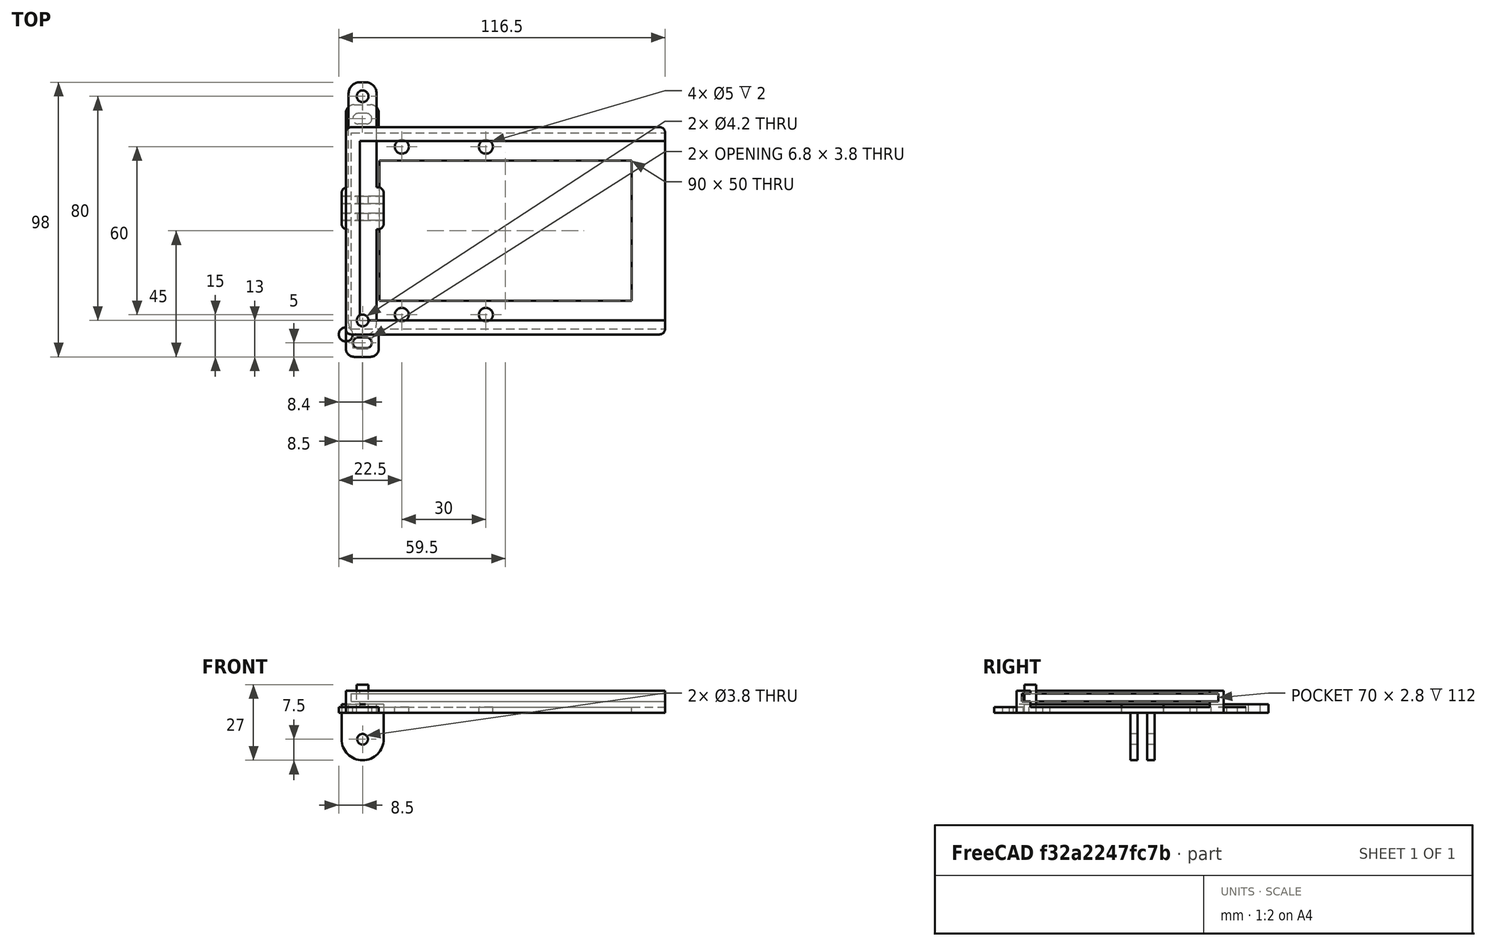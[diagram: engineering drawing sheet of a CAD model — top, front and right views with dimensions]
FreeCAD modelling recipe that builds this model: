
FCSTD DOCUMENT  (FreeCAD 0.19R23578 (Git))
Label: solar_110x70
License: All rights reserved
LicenseURL: http://en.wikipedia.org/wiki/All_rights_reserved
objects: Part::Box×6, Part::Fillet×3, Part::MultiFuse×3, Part::Cylinder×2, Part::FeaturePython×2, Part::Feature×2, Part::Cut×2, App::Part×2, Spreadsheet::Sheet×1
note: 18 computed .brp shape members not serialized (recipe doc carries the construction recipe); baked Part::Feature solids carry a one-line shape summary decoded from their .brp

FEATURE [Part::Box] Box  label="outer cube"
  AttacherType = Attacher::AttachEngine3D
  Height = 7.8
  Length = 114
  Width = 74
  expr: Height = <<p>>.bottom + <<p>>.bottom_space + <<p>>.size_z + <<p>>.top
  expr: Length = <<p>>.size_x + 2 * <<p>>.wall
  expr: Width = <<p>>.size_y + 2 * <<p>>.wall
FEATURE [Spreadsheet::Sheet] Spreadsheet  label="p"
  cells = A1=size_x; B1(size_x)==110mm; A2=size_y; B2(size_y)==70mm; A3=size_z; B3(size_z)==2.8mm; A4=wall; B4(wall)==2mm; A5=bottom_space; B5(bottom_space)==2mm; A6=top; B6(top)==1mm; A7=bottom; B7(bottom)==2mm; A8=pad; B8(pad)==10mm; A9=wire_hole_size; B9(wire_hole_r)==2.5mm; A10=side_lane; B10(side_lane)==3mm
FEATURE [Part::Box] Box001  label="bottom space cube"
  AttacherType = Attacher::AttachEngine3D
  Height = 2
  Length = 109
  Placement = pos=(5,5,2) rot=(0,0,1;0rad)
  Width = 64
  expr: Width = <<p>>.size_y - 2 * <<p>>.side_lane
  expr: Length = <<p>>.size_x - <<p>>.side_lane + <<p>>.wall
  expr: Height = <<p>>.bottom_space
  expr: .Placement.Base.x = <<p>>.wall + <<p>>.side_lane
  expr: .Placement.Base.y = <<p>>.wall + <<p>>.side_lane
  expr: .Placement.Base.z = <<p>>.bottom
FEATURE [Part::Box] Box002  label="panel extract cube"
  AttacherType = Attacher::AttachEngine3D
  Height = 2.8
  Length = 112
  Placement = pos=(2,2,4) rot=(0,0,1;0rad)
  Width = 70
  expr: .Placement.Base.z = <<p>>.bottom + <<p>>.bottom_space
  expr: .Placement.Base.y = <<p>>.wall
  expr: .Placement.Base.x = <<p>>.wall
  expr: Height = <<p>>.size_z
  expr: Length = <<p>>.size_x + <<p>>.wall
  expr: Width = <<p>>.size_y
FEATURE [Part::Box] Box003  label="panel face extract cube"
  AttacherType = Attacher::AttachEngine3D
  Height = 1
  Length = 109
  Placement = pos=(5,5,6.8) rot=(0,0,1;0rad)
  Width = 64
  expr: Width = <<p>>.size_y - 2 * <<p>>.side_lane
  expr: Length = <<p>>.size_x - <<p>>.side_lane + <<p>>.wall
  expr: Height = <<p>>.top
  expr: .Placement.Base.x = <<p>>.wall + <<p>>.side_lane
  expr: .Placement.Base.y = <<p>>.wall + <<p>>.side_lane
  expr: .Placement.Base.z = <<p>>.bottom + <<p>>.bottom_space + <<p>>.size_z
FEATURE [Part::Box] Box004  label="bottom hole cube"
  AttacherType = Attacher::AttachEngine3D
  Height = 2
  Length = 90
  Placement = pos=(12,12,0) rot=(0,0,1;0rad)
  Width = 50
  expr: .Placement.Base.y = <<p>>.wall + <<p>>.pad
  expr: .Placement.Base.x = <<p>>.wall + <<p>>.pad
  expr: Height = <<p>>.bottom
  expr: Length = <<p>>.size_x - 2 * <<p>>.pad
  expr: Width = <<p>>.size_y - 2 * <<p>>.pad
FEATURE [Part::Fillet] Fillet  label="outer fillet"
  Base = -> Box
  Edges = 4 edges r=2: [Edge1,Edge3,Edge5,Edge7]
FEATURE [Part::Cylinder] Cylinder  label="wire hole"
  Angle = 360
  AttacherType = Attacher::AttachEngine3D
  Height = 2
  Radius = 2.5
  expr: Radius = <<p>>.wire_hole_r
  expr: Height = <<p>>.bottom
FEATURE [Part::FeaturePython] Array  label="wire hole array"  # Draft array (typed FeaturePython)
  Angle = 360
  ArrayType = 0
  Axis = (0,0,1)
  Base = -> Cylinder
  Center = (0,0,0)
  Count = 4
  ExpandArray = false
  Fuse = false
  IntervalAxis = (0,0,0)
  IntervalX = (30,0,0)
  IntervalY = (0,60,0)
  IntervalZ = (0,0,100)
  NumberCircles = 3
  NumberPolar = 5
  NumberX = 2
  NumberY = 2
  NumberZ = 1
  Placement = pos=(20,7,0) rot=(0,0,1;0rad)
  PlacementList = 4 placements: [(0,0,0),(0,60,0),(30,0,0),(30,60,0)]
  RadialDistance = 50
  ScaleList = (4) [(1,1,1),(1,1,1),(1,1,1),(1,1,1)]
  Symmetry = 1
  TangentialDistance = 25
  expr: .IntervalY.y = <<p>>.size_y - 2 * <<p>>.pad + 4 * <<p>>.wire_hole_r
  expr: .Placement.Base.y = <<p>>.wall + <<p>>.pad - 2 * <<p>>.wire_hole_r
FEATURE [Part::MultiFuse] Fusion  label="extract fusion"
  Shapes = -> [Box001,Box002,Box003,Box004,Array]
FEATURE [Part::Feature] Cut002002  label="attach plane y dir002"
  Placement = pos=(0,-8,0) rot=(0,0,1;0rad)
  shape: bbox 11.8 x 90 x 2 mm, 20 faces (baked)
FEATURE [Part::MultiFuse] Fusion001  label="body fusion"
  Shapes = -> [Fillet,Cut002002]
FEATURE [Part::Cut] Cut  label="body cut"
  Base = -> Fusion001
  Tool = -> Fusion
FEATURE [App::Part] Part  label="body part"
  Group = -> [Cut]
  Origin = -> Origin
FEATURE [Part::Feature] Cut001001001  label="side 2"
  Placement = pos=(6,45,3) rot=(0,1,0;3.14159rad)
  shape: bbox 15 x 15 x 20 mm, 16 faces (baked)
FEATURE [Part::Cylinder] Cylinder001  label="insert hole"
  Angle = 360
  AttacherType = Attacher::AttachEngine3D
  Height = 10
  Placement = pos=(6,5,0) rot=(0,0,1;0rad)
  Radius = 2.1
FEATURE [Part::Box] Box005  label="plane cube"
  AttacherType = Attacher::AttachEngine3D
  Height = 3
  Length = 10
  Placement = pos=(1,0,0) rot=(0,0,1;0rad)
  Width = 90
FEATURE [Part::Fillet] Fillet001  label="plane fillet"
  Base = -> Box005
  Edges = 4 edges r=4: [Edge1,Edge3,Edge5,Edge7]
FEATURE [Part::FeaturePython] Array001  label="insert hole array"  # Draft array (typed FeaturePython)
  Angle = 360
  ArrayType = 0
  Axis = (0,0,1)
  Base = -> Cylinder001
  Center = (0,0,0)
  Count = 2
  ExpandArray = false
  Fuse = false
  IntervalAxis = (0,0,0)
  IntervalX = (100,0,0)
  IntervalY = (0,80,0)
  IntervalZ = (0,0,100)
  NumberCircles = 3
  NumberPolar = 5
  NumberX = 1
  NumberY = 2
  NumberZ = 1
  PlacementList = 2 placements: [(6,5,0),(6,85,0)]
  RadialDistance = 50
  ScaleList = (2) [(1,1,1),(1,1,1)]
  Symmetry = 1
  TangentialDistance = 25
FEATURE [Part::Fillet] Fillet002  label="side 2 fillet"
  Base = -> Cut001001001
  Edges = 4 edges r=2: [Edge1,Edge11,Edge13,Edge42]
FEATURE [Part::MultiFuse] Fusion002  label="attachment fusion"
  Shapes = -> [Fillet001,Fillet002]
FEATURE [Part::Cut] Cut001001002  label="attachment cut"
  Base = -> Fusion002
  Tool = -> Array001
FEATURE [App::Part] Part001  label="attachment part"
  Group = -> [Cut001001002]
  Origin = -> Origin001
  Placement = pos=(0,-8,0) rot=(0,0,1;0rad)
